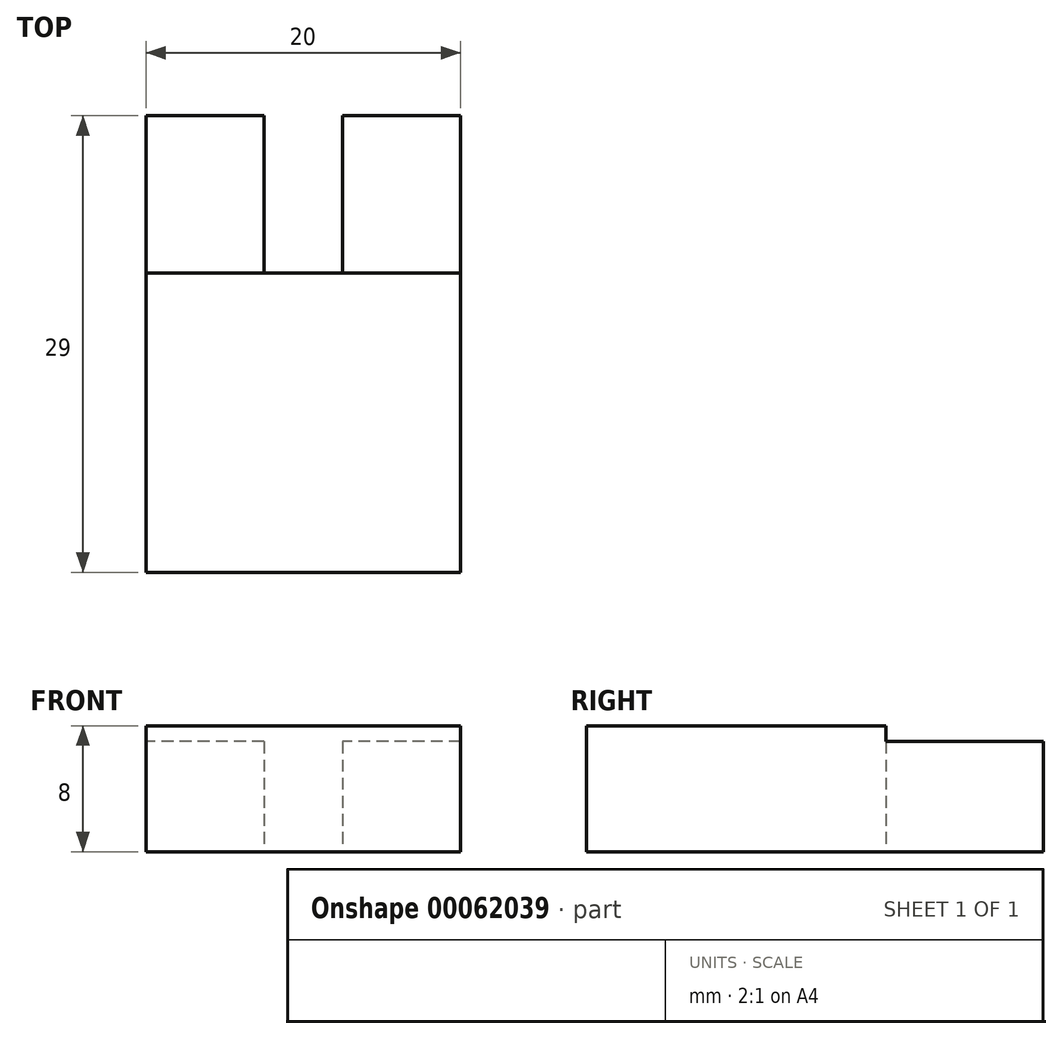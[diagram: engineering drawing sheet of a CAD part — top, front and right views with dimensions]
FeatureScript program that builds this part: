
annotation { "Feature Type Name" : "Feature", "Feature Type Description" : "" }
export const myFeature = defineFeature(function(context is Context, id is Id, definition is map)
    precondition{}
    {
        {
            var Q0;
            Q0=qCreatedBy(makeId("Top.planeOp"),FACE);
            var sketch = newSketch(context, id + "F0", { "sketchPlane" : qUnion([Q0])});
            skLineSegment(sketch, "E0.rect.bottom", {"start": v(10, -14.5) * mm, "end": v(-10, -14.5) * mm});
            skLineSegment(sketch, "E0.rect.top", {"start": v(10, 14.5) * mm, "end": v(-10, 14.5) * mm});
            skLineSegment(sketch, "E0.rect.left", {"start": v(10, -14.5) * mm, "end": v(10, 14.5) * mm});
            skLineSegment(sketch, "E0.rect.right", {"start": v(-10, -14.5) * mm, "end": v(-10, 14.5) * mm});
            skPoint(sketch, "E0.rect.middle", {"position": v(0, 0) * mm});
            skLineSegment(sketch, "E1.bottom", {"start": v(-2.5, 14.5) * mm, "end": v(2.5, 14.5) * mm});
            skLineSegment(sketch, "E1.top", {"start": v(-2.5, 4.5) * mm, "end": v(2.5, 4.5) * mm});
            skLineSegment(sketch, "E1.left", {"start": v(-2.5, 14.5) * mm, "end": v(-2.5, 4.5) * mm});
            skLineSegment(sketch, "E1.right", {"start": v(2.5, 14.5) * mm, "end": v(2.5, 4.5) * mm});
            skLineSegment(sketch, "E2", {"start": v(0, 0) * mm, "end": v(-2.5, 0) * mm, "construction": true});
            skLineSegment(sketch, "E3", {"start": v(0, 0) * mm, "end": v(2.5, 0) * mm, "construction": true});
            skSolve(sketch);
        }
        {
            var Q0;
            Q0=makeQuery(id+"F0.imprint","IMPRINT",FACE,{"disambiguationData":[TD([[makeQuery(id+"F0.imprint","IMPRINT",EDGE,{"derivedFrom":sQuery(id+"F0.wireOp",EDGE,"E0.rect.bottom")}),-1.0]])]});
            extrude(context, id + "F1", {"entities" : qUnion([Q0]), "depth" : 8 * mm});
        }
        {
            var Q0;
            Q0=makeQuery(id+"F1.opExtrude","SWEPT_FACE",FACE,{"disambiguationData":[OSD([sQuery(id+"F0.wireOp",EDGE,"E0.rect.right")])]});
            var sketch = newSketch(context, id + "F2", { "sketchPlane" : qUnion([Q0])});
            skLineSegment(sketch, "E4", {"start": v(-4.5, 8) * mm, "end": v(-4.5, 7) * mm});
            skLineSegment(sketch, "E5", {"start": v(-4.5, 7) * mm, "end": v(-14.5, 7) * mm});
            skSolve(sketch);
        }
        {
            var Q0;
            {var subQ0=sQuery(id+"F2.wireOp",EDGE,"E4");Q0=makeQuery(id+"F2.imprint","IMPRINT",FACE,{"disambiguationData":[TD([[makeQuery(id+"F2.imprint","IMPRINT",EDGE,{"derivedFrom":subQ0}),-1.0]])]});}
            extrude(context, id + "F3", {"entities" : qUnion([Q0]), "operationType" : NewBodyOperationType.REMOVE, "oppositeDirection" : true, "depth" : 25 * mm});
        }
    });
